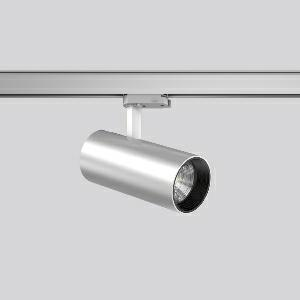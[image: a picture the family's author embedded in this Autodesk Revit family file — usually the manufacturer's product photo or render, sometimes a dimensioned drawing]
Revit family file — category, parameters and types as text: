
# Revit family: deecos_s_mini_742200_004_2_76_1944
name_source: partatom
category: Lighting Fixtures
units: mm (PartAtom-declared; Revit-internal decimal feet)

## family parameters
Cut with Voids When Loaded = No
Host = Face
Light Source = No
Part Type = Normal
Room Calculation Point = No
Round Connector Dimension = Use Diameter
Shared = No

## types (1)
- DEECOS S mini (1 x LED Modul 927, 1900 lm, 2700)
    Apparent Load = 20 VA
    Approval mark = CE
    CIE Flux Codes = 98 100 100 100 100
    Color Rendering = 92
    Color Temperature = 2700
    Default Elevation = 1800 mm
    Description = Series: DEECOS S mini
LED surface-mounted projector in modern design with no visible cooling ribs. Housing: die-cast aluminium, powder-coated. Rotation range: 356°. Swivel range: 90°. Black plastic ring and recessed LED to prevent glare from the side. Optical assembly with lens made of plastic (polycarbonate) for the best homogeneous light distribution - can be changed without tools. Best colour rendering index Ra>90. With adapter for RZB 3-circuit DALI tracks. Suitable for Track on ceiling, Wall track. High quality converter without flickering and stroboscopic effect. The following accessories can be mounted without use of tools: interchangeable lenses, decorative glasses, honeycomb louvre, clear and frosted diffusers, white interchangeable plastic ring. 
Colour: silver
Diameter: 87 mm
Height: 214 mm
Lamp: LED
Socket: without socket
Colour temperature: 2700K
Colour rendering index (CRI): 92
System power: 20 W
Rated luminous flux: 1900 lm
Luminous efficiency: 95 lm/W
Control gear: Converter, dimmable, DALI
Protection class: I
Type of protection: IP 20
    Height = 214 mm
    Lamp = 1 x LED Modul 927
    Lamp Light Flux = 1900 lm
    Lamp count = 1
    Length = 87 mm
    Lifetime = 50000 h
    Luminous efficacy = 95 lm/W
    Manufacturer = RZB
    ModVariant = No
    Model = 742200.004.2.76
    Mounting Place = Ceiling
    Mounting Type = Rail mounted
    Number of Poles = 1
    OnlyDefault = Yes
    Power Factor = 1
    Product Name = DEECOS S mini
    Product group = Track mounted projectors
    ProductGroupID = 301
    Protection Class = Protection class I
    Protection Degree = IP 20
    RLX_Detail_Level = 1
    RLX_Emergency_Light_Flux = 0 lm
    RLX_Emergency_Type = 0
    RLX_Emergency_Type_DB = No
    RlxData = <blob elided: 37361 chars, md5=50f4974e>
    Socket = socket
    Standby Power = 0 W
    System Light Flux = 1900 lm
    System Power = 20 W
    Type Comments = Product without accessories
    Type Image = 741930.004.jpg
    URL = http://relux.com
    VarID = ---
    Voltage = 230 V
    Voltage Range = 220-240 V
    Weight = 0.00 kg
    Width = 0 mm  [stored 0 ft]

note: [stored X ft] marks values corroborated as IEEE doubles in the binary element streams (Revit-internal decimal feet)

## geometry (parser evidence)
native form markers: Blend x4, Sweep x13
no freeform markers — native parametric forms only
